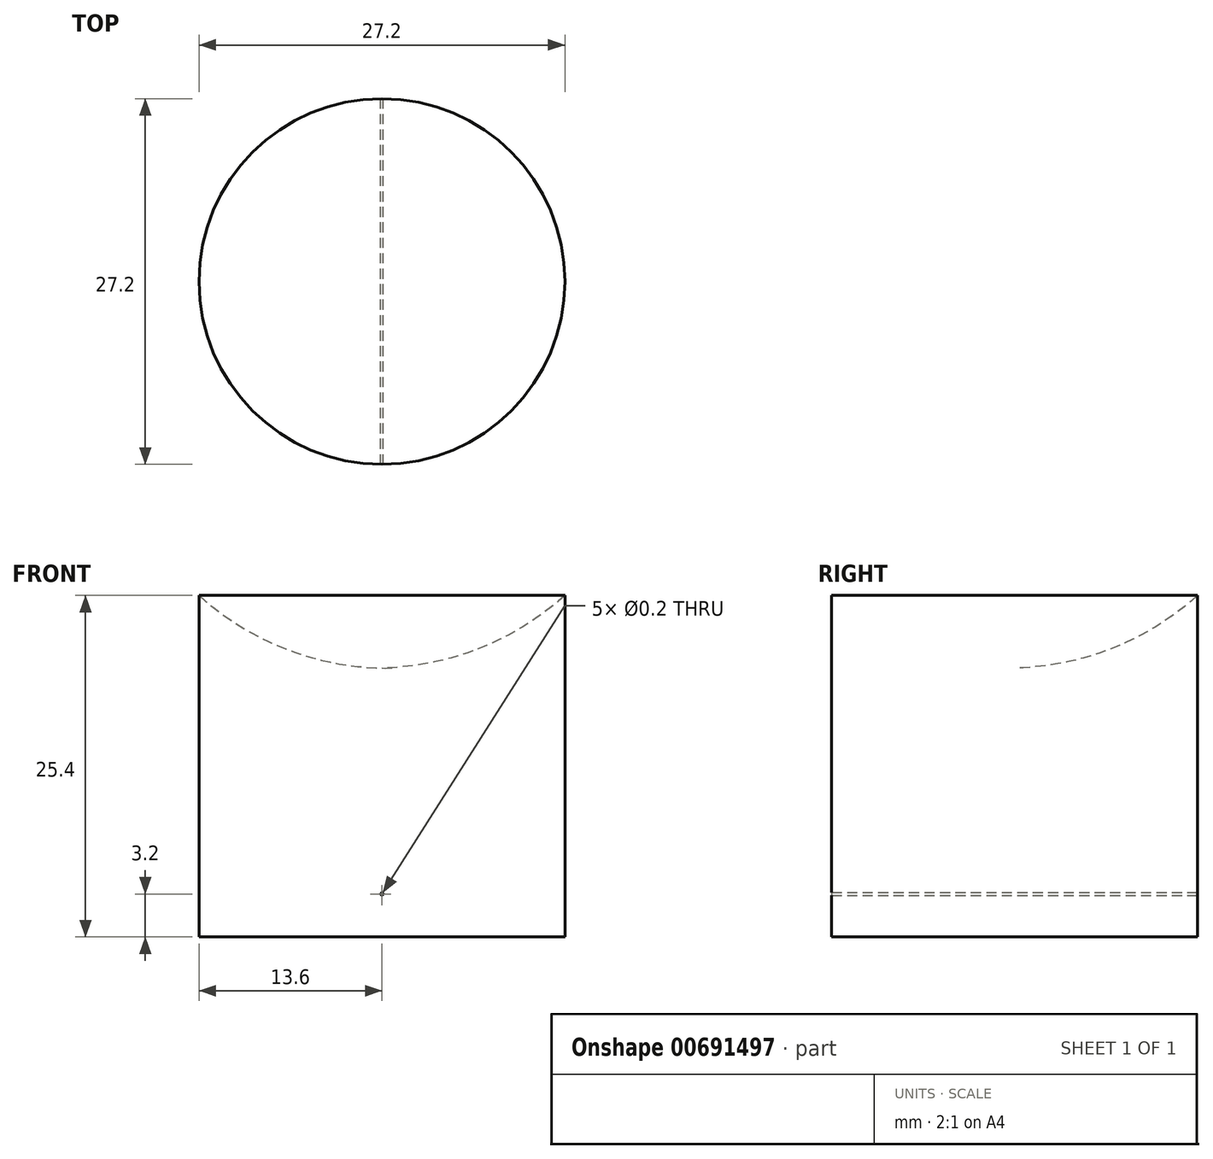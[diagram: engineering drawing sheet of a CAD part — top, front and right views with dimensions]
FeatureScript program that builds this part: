
annotation { "Feature Type Name" : "Feature", "Feature Type Description" : "" }
export const myFeature = defineFeature(function(context is Context, id is Id, definition is map)
    precondition{}
    {
        {
            var Q0;
            Q0=qCreatedBy(makeId("Front.planeOp"),FACE);
            var sketch = newSketch(context, id + "F0", { "sketchPlane" : qUnion([Q0])});
            skLineSegment(sketch, "E0", {"start": v(0, 0) * mm, "end": v(-13.6, 0) * mm});
            skLineSegment(sketch, "E1", {"start": v(-13.6, 0) * mm, "end": v(-13.6, 25.4) * mm});
            skArc(sketch, "E2", {"start": v(-13.6, 25.4) * mm, "mid": v(-7.29, 21.48) * mm, "end": v(0, 20) * mm});
            skLineSegment(sketch, "E3", {"start": v(0, 0) * mm, "end": v(0, 20) * mm});
            skSolve(sketch);
        }
        {
            var Q0;
            Q0=qCreatedBy(makeId("Front.planeOp"),FACE);
            var sketch = newSketch(context, id + "F1", { "sketchPlane" : qUnion([Q0])});
            skLineSegment(sketch, "E4", {"start": v(0, 0) * mm, "end": v(0, -10.03) * mm});
            skSolve(sketch);
        }
        {
            var Q0;
            Q0 = qSketchRegion(id + "F0", true);
            var Q1;
            Q1=sQuery(id+"F1.wireOp",EDGE,"E4");
            revolve(context, id + "F2", {"entities" : qUnion([Q0]), "axis" : qUnion([Q1]), "revolveType" : RevolveType.FULL});
        }
        {
            var Q0;
            Q0=qCreatedBy(makeId("Front.planeOp"),FACE);
            var sketch = newSketch(context, id + "F3", { "sketchPlane" : qUnion([Q0])});
            skCircle(sketch, "E5", {"center": v(0, 3.2) * mm, "radius": 0.1 * mm});
            skSolve(sketch);
        }
        {
            var Q0;
            Q0 = qSketchRegion(id + "F3", true);
            extrude(context, id + "F4", {"entities" : qUnion([Q0]), "operationType" : NewBodyOperationType.REMOVE, "endBound" : BoundingType.SYMMETRIC, "depth" : 60 * mm, "offsetDistance" : 25 * mm});
        }
    });
